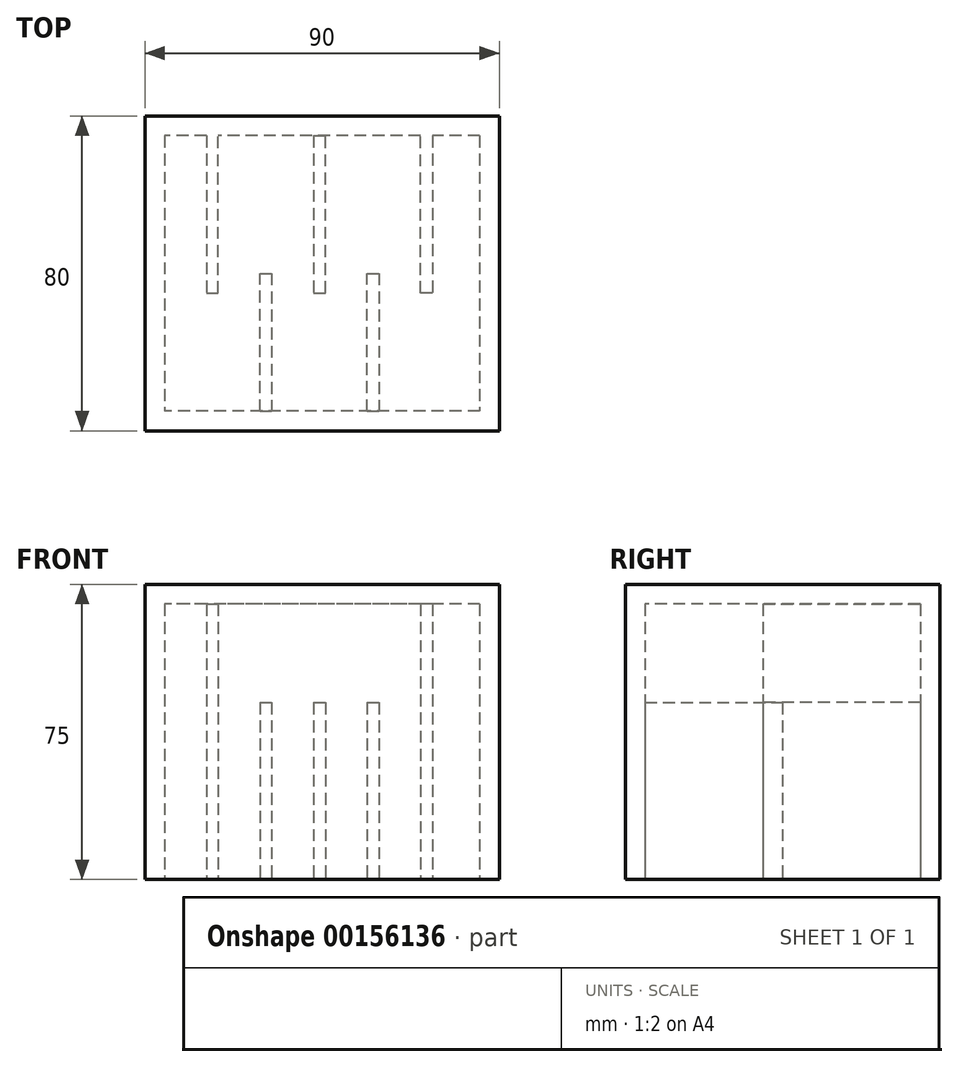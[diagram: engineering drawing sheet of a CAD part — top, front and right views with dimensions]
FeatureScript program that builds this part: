
annotation { "Feature Type Name" : "Feature", "Feature Type Description" : "" }
export const myFeature = defineFeature(function(context is Context, id is Id, definition is map)
    precondition{}
    {
        {
            var Q0;
            Q0=qCreatedBy(makeId("Top.planeOp"),FACE);
            var sketch = newSketch(context, id + "F0", { "sketchPlane" : qUnion([Q0])});
            skLineSegment(sketch, "E0.bottom", {"start": v(45, 40) * mm, "end": v(-45, 40) * mm});
            skLineSegment(sketch, "E0.top", {"start": v(45, -40) * mm, "end": v(-45, -40) * mm});
            skLineSegment(sketch, "E0.left", {"start": v(45, 40) * mm, "end": v(45, -40) * mm});
            skLineSegment(sketch, "E0.right", {"start": v(-45, 40) * mm, "end": v(-45, -40) * mm});
            skPoint(sketch, "E0.middle", {"position": v(0, 0) * mm});
            skLineSegment(sketch, "E1.bottom", {"start": v(40, 35) * mm, "end": v(28, 35) * mm});
            skLineSegment(sketch, "E1.top", {"start": v(40, -35) * mm, "end": v(14.4, -35) * mm});
            skLineSegment(sketch, "E1.left", {"start": v(40, 35) * mm, "end": v(40, -35) * mm});
            skLineSegment(sketch, "E1.right", {"start": v(-40, 35) * mm, "end": v(-40, -35) * mm});
            skLineSegment(sketch, "E2", {"start": v(-29.4, 35) * mm, "end": v(-29.4, -5) * mm});
            skLineSegment(sketch, "E3", {"start": v(-29.4, -5) * mm, "end": v(-26.4, -5) * mm});
            skLineSegment(sketch, "E4", {"start": v(-26.4, -5) * mm, "end": v(-26.4, 35) * mm});
            skLineSegment(sketch, "E5", {"start": v(28, 35) * mm, "end": v(28, -5) * mm});
            skLineSegment(sketch, "E6", {"start": v(28, -5) * mm, "end": v(25, -5) * mm});
            skLineSegment(sketch, "E7", {"start": v(25, -5) * mm, "end": v(25, 35) * mm});
            skLineSegment(sketch, "E8.trimOffspring", {"start": v(-29.4, 35) * mm, "end": v(-40, 35) * mm});
            skLineSegment(sketch, "E9.trimOffspring", {"start": v(25, 35) * mm, "end": v(0.8, 35) * mm});
            skLineSegment(sketch, "E10", {"start": v(-2.2, 35) * mm, "end": v(-2.2, -5) * mm});
            skLineSegment(sketch, "E11", {"start": v(-2.2, -5) * mm, "end": v(0.8, -5) * mm});
            skLineSegment(sketch, "E12", {"start": v(0.8, -5) * mm, "end": v(0.8, 35) * mm});
            skLineSegment(sketch, "E13", {"start": v(-15.8, -35) * mm, "end": v(-15.8, 0) * mm});
            skLineSegment(sketch, "E14", {"start": v(-15.8, 0) * mm, "end": v(-12.8, 0) * mm});
            skLineSegment(sketch, "E15", {"start": v(-12.8, 0) * mm, "end": v(-12.8, -35) * mm});
            skLineSegment(sketch, "E16", {"start": v(11.4, -35) * mm, "end": v(11.4, 0) * mm});
            skLineSegment(sketch, "E17", {"start": v(11.4, 0) * mm, "end": v(14.4, 0) * mm});
            skLineSegment(sketch, "E18", {"start": v(14.4, 0) * mm, "end": v(14.4, -35) * mm});
            skLineSegment(sketch, "E19.trimOffspring", {"start": v(-2.2, 35) * mm, "end": v(-26.4, 35) * mm});
            skLineSegment(sketch, "E20.trimOffspring", {"start": v(-15.8, -35) * mm, "end": v(-40, -35) * mm});
            skLineSegment(sketch, "E21.trimOffspring", {"start": v(11.4, -35) * mm, "end": v(-12.8, -35) * mm});
            skLineSegment(sketch, "E22", {"start": v(-2.2, 35) * mm, "end": v(0.8, 35) * mm});
            skLineSegment(sketch, "E23", {"start": v(11.4, -35) * mm, "end": v(14.4, -35) * mm});
            skLineSegment(sketch, "E24", {"start": v(-15.8, -35) * mm, "end": v(-12.8, -35) * mm});
            skSolve(sketch);
        }
        {
            var Q0;
            Q0=makeQuery(id+"F0.imprint","IMPRINT",FACE,{"disambiguationData":[TD([[makeQuery(id+"F0.imprint","IMPRINT",EDGE,{"derivedFrom":sQuery(id+"F0.wireOp",EDGE,"E13")}),-1.0]])]});
            var Q1;
            Q1=makeQuery(id+"F0.imprint","IMPRINT",FACE,{"disambiguationData":[TD([[makeQuery(id+"F0.imprint","IMPRINT",EDGE,{"derivedFrom":sQuery(id+"F0.wireOp",EDGE,"E10")}),1.0]])]});
            var Q2;
            Q2=makeQuery(id+"F0.imprint","IMPRINT",FACE,{"disambiguationData":[TD([[makeQuery(id+"F0.imprint","IMPRINT",EDGE,{"derivedFrom":sQuery(id+"F0.wireOp",EDGE,"E16")}),-1.0]])]});
            var Q3;
            Q3=sQuery(id+"F0.wireOp",EDGE,"E22");
            var Q4;
            Q4=sQuery(id+"F0.wireOp",EDGE,"E12");
            var Q5;
            Q5=sQuery(id+"F0.wireOp",EDGE,"E10");
            var Q6;
            Q6=sQuery(id+"F0.wireOp",EDGE,"E11");
            var Q7;
            Q7=sQuery(id+"F0.wireOp",EDGE,"E14");
            var Q8;
            Q8=sQuery(id+"F0.wireOp",EDGE,"E15");
            var Q9;
            Q9=sQuery(id+"F0.wireOp",EDGE,"E13");
            var Q10;
            Q10=sQuery(id+"F0.wireOp",EDGE,"E17");
            var Q11;
            Q11=sQuery(id+"F0.wireOp",EDGE,"E16");
            var Q12;
            Q12=sQuery(id+"F0.wireOp",EDGE,"E18");
            var Q13;
            Q13=sQuery(id+"F0.wireOp",EDGE,"E24");
            var Q14;
            Q14=sQuery(id+"F0.wireOp",EDGE,"E23");
            extrude(context, id + "F1", {"entities" : qUnion([Q0, Q1, Q2]), "surfaceEntities" : qUnion([Q3, Q4, Q5, Q6, Q7, Q8, Q9, Q10, Q11, Q12, Q13, Q14]), "depth" : 45 * mm});
        }
        {
            var Q0;
            Q0=makeQuery(id+"F0.imprint","IMPRINT",FACE,{"disambiguationData":[TD([[makeQuery(id+"F0.imprint","IMPRINT",EDGE,{"derivedFrom":sQuery(id+"F0.wireOp",EDGE,"E0.bottom")}),1.0]])]});
            extrude(context, id + "F2", {"entities" : qUnion([Q0]), "depth" : 70 * mm});
        }
        {
            var Q0;
            Q0=makeQuery(id+"F2.opExtrude","CAP_FACE",FACE,{"disambiguationData":[OSD([sQuery(id+"F0.wireOp",EDGE,"E0.bottom"),sQuery(id+"F0.wireOp",EDGE,"E0.top"),sQuery(id+"F0.wireOp",EDGE,"E0.left"),sQuery(id+"F0.wireOp",EDGE,"E0.right"),sQuery(id+"F0.wireOp",EDGE,"E1.bottom"),sQuery(id+"F0.wireOp",EDGE,"E1.top"),sQuery(id+"F0.wireOp",EDGE,"E1.left"),sQuery(id+"F0.wireOp",EDGE,"E1.right"),sQuery(id+"F0.wireOp",EDGE,"E2"),sQuery(id+"F0.wireOp",EDGE,"E3"),sQuery(id+"F0.wireOp",EDGE,"E4"),sQuery(id+"F0.wireOp",EDGE,"E5"),sQuery(id+"F0.wireOp",EDGE,"E6"),sQuery(id+"F0.wireOp",EDGE,"E7"),sQuery(id+"F0.wireOp",EDGE,"E8.trimOffspring"),sQuery(id+"F0.wireOp",EDGE,"E9.trimOffspring"),sQuery(id+"F0.wireOp",EDGE,"E19.trimOffspring"),sQuery(id+"F0.wireOp",EDGE,"E20.trimOffspring"),sQuery(id+"F0.wireOp",EDGE,"E21.trimOffspring"),sQuery(id+"F0.wireOp",EDGE,"E22"),sQuery(id+"F0.wireOp",EDGE,"E23"),sQuery(id+"F0.wireOp",EDGE,"E24")])],"isStart":false});
            var sketch = newSketch(context, id + "F3", { "sketchPlane" : qUnion([Q0])});
            skLineSegment(sketch, "E25.bottom", {"start": v(45, 40) * mm, "end": v(-45, 40) * mm});
            skLineSegment(sketch, "E25.top", {"start": v(45, -40) * mm, "end": v(-45, -40) * mm});
            skLineSegment(sketch, "E25.left", {"start": v(45, 40) * mm, "end": v(45, -40) * mm});
            skLineSegment(sketch, "E25.right", {"start": v(-45, 40) * mm, "end": v(-45, -40) * mm});
            skPoint(sketch, "E25.middle", {"position": v(0, 0) * mm});
            skSolve(sketch);
        }
        {
            var Q0;
            Q0 = qSketchRegion(id + "F3", true);
            extrude(context, id + "F4", {"entities" : qUnion([Q0]), "operationType" : NewBodyOperationType.ADD, "depth" : 5 * mm});
        }
    });
